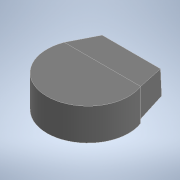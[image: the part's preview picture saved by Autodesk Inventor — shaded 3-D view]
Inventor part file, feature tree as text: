
AUTODESK INVENTOR PART (.ipt)
format: ipt  version: 2022 (Build 260153000, 153)  size: 229,888 bytes
history: native  units: mm
features: extrude x10, sketch x10, chamfer x2, plane x1
ambient origin geometry x8: Origin, YZ Plane, XZ Plane, XY Plane, X Axis, Y Axis, Z Axis, Center Point
bodies: Solid1 (feature_tree)
feature tree (23):
  extrude  "Extrusion1"  Depth=48.0mm
  chamfer  "Chamfer1"  Distance=30.0mm
  chamfer  "Chamfer2"  Distance=2.0mm Angle=45.0deg
  extrude  "Extrusion2"  Depth=2.0mm
  extrude  "Extrusion3"  Depth=30.0mm
  extrude  "Extrusion4"  Depth=4.0mm
  extrude  "Extrusion5"  Depth=30.0mm
  extrude  "Extrusion6"  Depth=2.0mm
  extrude  "Extrusion7"  Depth=2.0mm
  extrude  "Extrusion8"  Depth=5.0mm TaperAngle=0.0deg
  plane  "Work Plane1"
  extrude  "Extrusion9"  Depth=5.0mm
  extrude  "Extrusion10"  Depth=2.0mm
  sketch  "Sketch1"  dims[d0=87.0mm d1=48.0mm]
  sketch  "Sketch2"  dims[d2=30.5mm]
  sketch  "Sketch3"  dims[d3=30.5mm]
  sketch  "Sketch4"  dims[d4=59.0mm]
  sketch  "Sketch5"  dims[d5=2.0mm]
  sketch  "Sketch6"  dims[d6=2.0mm d7=30.0mm d8=0.0mm d9=2.0mm d10=30.0mm d11=45.0deg]
  sketch  "Sketch7"  dims[d12=4.0mm d13=30.5mm d14=45.0deg d15=2.0mm]
  sketch  "Sketch8"  dims[d16=59.0mm d17=30.0mm]
  sketch  "Sketch12"  dims[d18=64.0mm d19=4.0mm]
  sketch  "Sketch13"  dims[d20=4.0mm d21=0.0mm d22=30.0mm d24=65.0mm d25=2.5mm d26=5.0mm d27=0.0mm d28=5.0mm d29=3.5mm d30=5.0mm d31=0.0mm d32=30.0mm d33=0.0mm d34=10.0mm d35=0.0mm d36=2.5mm d37=5.0mm d38=0.0mm d39=3.0mm d40=3.0mm d41=5.0mm d42=0.0mm d43=3.5mm d44=3.5mm d47=3.0mm d48=3.0mm d49=3.0mm d50=3.0mm d51=50.0mm d52=10.0mm d53=0.0mm d54=0.0mm d55=5.0mm d56=5.0mm d57=5.0mm d58=5.0mm d59=4.5mm d60=57.0mm d61=2.0mm d62=0.0mm d63=0.0mm]
